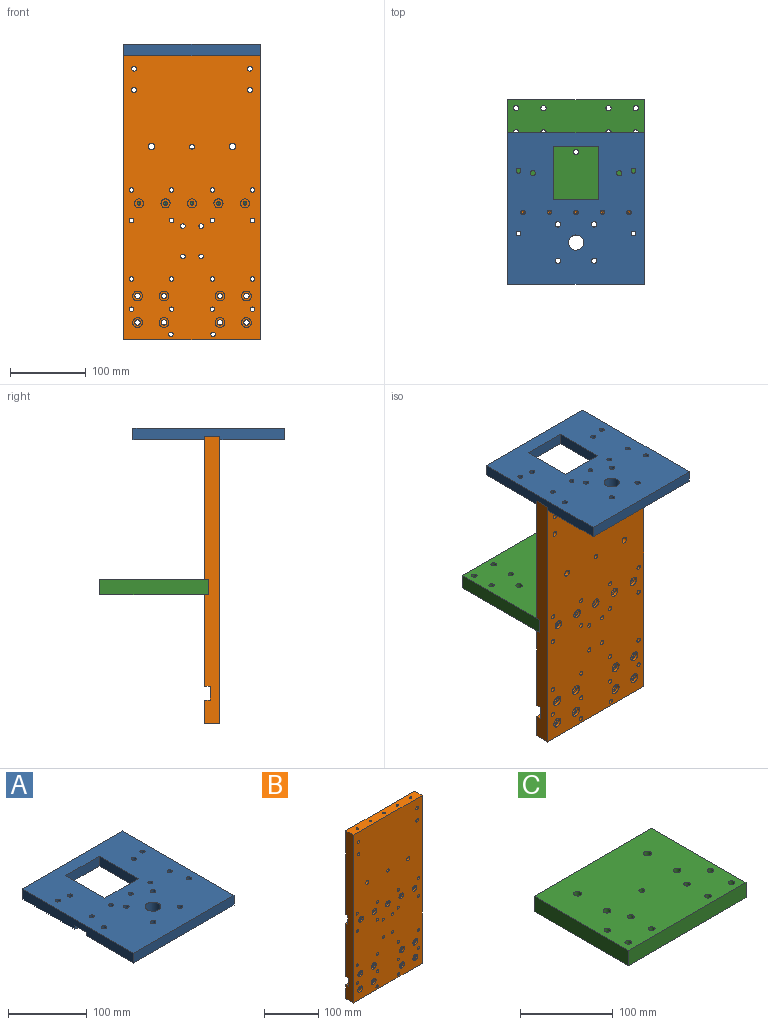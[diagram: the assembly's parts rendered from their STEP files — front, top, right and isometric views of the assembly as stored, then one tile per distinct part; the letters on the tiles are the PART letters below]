
ASSEMBLY  parts=3 mates=1
PART A: 30 faces, bbox 180x200x15 mm
  f0: plane 180x95mm, normal (0,0,-1), area 12761mm2, adj f1,f3,f4,f8,f11,f12,f13,f14
  f1: plane 200x15mm, normal (-1,0,0), area 2900mm2, adj f0,f2,f4,f5,f6,f7,f8,f9
  f2: plane 180x15mm, normal (0,-1,0), area 2700mm2, adj f1,f3,f5,f6
  f3: plane 200x15mm, normal (1,0,0), area 2900mm2, adj f0,f2,f4,f5,f6,f7,f8,f9
  f4: plane 180x15mm, normal (0,1,0), area 2700mm2, adj f0,f1,f3,f5
  f5: plane 200x180mm, normal (0,0,1), area 30985.2mm2, adj f1,f2,f3,f4,f10,f11,f12,f13
  f6: plane 180x85mm, normal (0,0,-1), area 14765.5mm2, adj f1,f2,f3,f7,f10,f22,f23,f24
  f7: plane 180x5mm, normal (0,1,0), area 900mm2, adj f1,f3,f6,f9
  f8: plane 180x5mm, normal (0,-1,0), area 900mm2, adj f0,f1,f3,f9
  f9: plane 180x20mm, normal (0,0,-1), area 3458.6mm2, adj f1,f3,f7,f8,f15,f16,f17,f18
  f10: cylinder r=10mm len=20mm, axis (0,0,1), area 942.5mm2, adj f5,f6
  f11: plane 70x15mm, normal (1,0,0), area 1050mm2, adj f0,f5,f12,f14
  f12: plane 60x15mm, normal (0,1,0), area 900mm2, adj f0,f5,f11,f13
  f13: plane 70x15mm, normal (-1,0,0), area 1050mm2, adj f0,f5,f12,f14
  f14: plane 60x15mm, normal (0,-1,0), area 900mm2, adj f0,f5,f11,f13
  f15: cylinder r=3mm len=10mm, axis (0,0,-1), area 188.5mm2, adj f5,f9
  f16: cylinder r=3mm len=10mm, axis (0,0,-1), area 188.5mm2, adj f5,f9
  f17: cylinder r=3mm len=10mm, axis (0,0,-1), area 188.5mm2, adj f5,f9
  f18: cylinder r=3mm len=10mm, axis (0,0,-1), area 188.5mm2, adj f5,f9
  f19: cylinder r=3mm len=10mm, axis (0,0,-1), area 188.5mm2, adj f5,f9
  f20: cylinder r=3.4mm len=15mm, axis (0,0,1), area 320.4mm2, adj f0,f5
  f21: cylinder r=3.4mm len=15mm, axis (0,0,1), area 320.4mm2, adj f0,f5
  f22: cylinder r=3.5mm len=15mm, axis (0,0,1), area 329.9mm2, adj f5,f6
  f23: cylinder r=3.5mm len=15mm, axis (0,0,1), area 329.9mm2, adj f5,f6
  f24: cylinder r=3.5mm len=15mm, axis (0,0,1), area 329.9mm2, adj f5,f6
  f25: cylinder r=3.5mm len=15mm, axis (0,0,1), area 329.9mm2, adj f5,f6
  f26: cylinder r=3.25mm len=15mm, axis (0,0,-1), area 306.3mm2, adj f0,f5
  f27: cylinder r=3.25mm len=15mm, axis (0,0,-1), area 306.3mm2, adj f0,f5
  f28: cylinder r=3.25mm len=15mm, axis (0,0,-1), area 306.3mm2, adj f5,f6
  f29: cylinder r=3.25mm len=15mm, axis (0,0,-1), area 306.3mm2, adj f5,f6
PART B: 92 faces, bbox 180x20x380 mm
  f0: plane 180x31mm, normal (0,1,0), area 5369.5mm2, adj f3,f5,f9,f15,f24,f27,f33,f36
  f1: plane 180x121mm, normal (0,1,0), area 21286.8mm2, adj f3,f5,f6,f7,f8,f10,f12,f16
  f2: plane 190x180mm, normal (0,1,0), area 33807.5mm2, adj f3,f4,f5,f13,f57,f58,f61,f63
  f3: plane 380x20mm, normal (1,0,0), area 7374mm2, adj f0,f1,f2,f4,f9,f11,f12,f13
  f4: plane 180x20mm, normal (0,0,1), area 3520.5mm2, adj f2,f3,f5,f11,f81,f83,f85,f87
  f5: plane 380x20mm, normal (-1,0,0), area 7374mm2, adj f0,f1,f2,f4,f9,f11,f12,f13
  f6: cylinder r=3mm len=20mm, axis (0,1,0), area 377mm2, adj f1,f11
  f7: cylinder r=3mm len=20mm, axis (0,1,0), area 377mm2, adj f1,f11
  f8: cylinder r=3mm len=20mm, axis (0,1,0), area 377mm2, adj f1,f11
  f9: plane 180x20mm, normal (0,0,-1), area 3600mm2, adj f0,f3,f5,f11
  f10: cylinder r=3mm len=20mm, axis (0,1,0), area 377mm2, adj f1,f11
  f11: plane 380x180mm, normal (0,-1,0), area 65871.2mm2, adj f3,f4,f5,f6,f7,f8,f9,f10
  f12: plane 180x5mm, normal (0,0,1), area 900mm2, adj f1,f3,f5,f14
  f13: plane 180x5mm, normal (0,0,-1), area 900mm2, adj f2,f3,f5,f14
  f14: plane 180x20mm, normal (0,1,0), area 3501.8mm2, adj f3,f5,f12,f13,f42,f45,f48,f51
  f15: plane 180x7mm, normal (0,0,1), area 1260mm2, adj f0,f3,f5,f17
  f16: plane 180x7mm, normal (0,0,-1), area 1260mm2, adj f1,f3,f5,f17
  f17: plane 180x18mm, normal (0,1,0), area 3126.9mm2, adj f3,f5,f15,f16,f66,f67,f70,f72
  f18: cylinder r=3.5mm len=16mm, axis (0,-1,0), area 351.9mm2, adj f1,f19
  f19: plane 13x13mm, normal (0,-1,0), area 94.2mm2, adj f18,f20
  f20: cylinder r=6.5mm len=13mm, axis (0,-1,0), area 163.4mm2, adj f11,f19
  f21: cylinder r=3.5mm len=16mm, axis (0,-1,0), area 351.9mm2, adj f1,f22
  f22: plane 13x13mm, normal (0,-1,0), area 94.2mm2, adj f21,f23
  f23: cylinder r=6.5mm len=13mm, axis (0,-1,0), area 163.4mm2, adj f11,f22
  f24: cylinder r=3.5mm len=16mm, axis (0,-1,0), area 351.9mm2, adj f0,f25
  f25: plane 13x13mm, normal (0,-1,0), area 94.2mm2, adj f24,f26
  f26: cylinder r=6.5mm len=13mm, axis (0,-1,0), area 163.4mm2, adj f11,f25
  f27: cylinder r=3.5mm len=16mm, axis (0,-1,0), area 351.9mm2, adj f0,f28
  f28: plane 13x13mm, normal (0,-1,0), area 94.2mm2, adj f27,f29
  f29: cylinder r=6.5mm len=13mm, axis (0,-1,0), area 163.4mm2, adj f11,f28
  f30: cylinder r=3.5mm len=16mm, axis (0,-1,0), area 351.9mm2, adj f1,f31
  f31: plane 13x13mm, normal (0,-1,0), area 94.2mm2, adj f30,f32
  f32: cylinder r=6.5mm len=13mm, axis (0,-1,0), area 163.4mm2, adj f11,f31
  f33: cylinder r=3.5mm len=16mm, axis (0,-1,0), area 351.9mm2, adj f0,f34
  f34: plane 13x13mm, normal (0,-1,0), area 94.2mm2, adj f33,f35
  f35: cylinder r=6.5mm len=13mm, axis (0,-1,0), area 163.4mm2, adj f11,f34
  f36: cylinder r=3.5mm len=16mm, axis (0,-1,0), area 351.9mm2, adj f0,f37
  f37: plane 13x13mm, normal (0,-1,0), area 94.2mm2, adj f36,f38
  f38: cylinder r=6.5mm len=13mm, axis (0,-1,0), area 163.4mm2, adj f11,f37
  f39: cylinder r=3.5mm len=16mm, axis (0,-1,0), area 351.9mm2, adj f1,f40
  f40: plane 13x13mm, normal (0,-1,0), area 94.2mm2, adj f39,f41
  f41: cylinder r=6.5mm len=13mm, axis (0,-1,0), area 163.4mm2, adj f11,f40
  f42: cylinder r=2.5mm len=11mm, axis (0,-1,0), area 172.8mm2, adj f14,f43
  f43: plane 12x12mm, normal (0,-1,0), area 93.5mm2, adj f42,f44
  f44: cylinder r=6mm len=12mm, axis (0,-1,0), area 150.8mm2, adj f11,f43
  f45: cylinder r=2.5mm len=11mm, axis (0,-1,0), area 172.8mm2, adj f14,f46
  f46: plane 12x12mm, normal (0,-1,0), area 93.5mm2, adj f45,f47
  f47: cylinder r=6mm len=12mm, axis (0,-1,0), area 150.8mm2, adj f11,f46
  f48: cylinder r=2.5mm len=11mm, axis (0,-1,0), area 172.8mm2, adj f14,f49
  f49: plane 12x12mm, normal (0,-1,0), area 93.5mm2, adj f48,f50
  f50: cylinder r=6mm len=12mm, axis (0,-1,0), area 150.8mm2, adj f11,f49
  f51: cylinder r=2.5mm len=11mm, axis (0,-1,0), area 172.8mm2, adj f14,f52
  f52: plane 12x12mm, normal (0,-1,0), area 93.5mm2, adj f51,f53
  f53: cylinder r=6mm len=12mm, axis (0,-1,0), area 150.8mm2, adj f11,f52
  f54: cylinder r=2.5mm len=11mm, axis (0,-1,0), area 172.8mm2, adj f14,f55
  f55: plane 12x12mm, normal (0,-1,0), area 93.5mm2, adj f54,f56
  f56: cylinder r=6mm len=12mm, axis (0,-1,0), area 150.8mm2, adj f11,f55
  f57: cylinder r=3mm len=20mm, axis (0,-1,0), area 377mm2, adj f2,f11
  f58: cylinder r=3mm len=20mm, axis (0,-1,0), area 377mm2, adj f2,f11
  f59: cylinder r=3mm len=20mm, axis (0,-1,0), area 377mm2, adj f1,f11
  f60: cylinder r=3mm len=20mm, axis (0,-1,0), area 377mm2, adj f1,f11
  f61: cylinder r=3mm len=20mm, axis (0,-1,0), area 377mm2, adj f2,f11
  f62: cylinder r=3mm len=20mm, axis (0,-1,0), area 377mm2, adj f1,f11
  f63: cylinder r=3mm len=20mm, axis (0,-1,0), area 377mm2, adj f2,f11
  f64: cylinder r=3mm len=20mm, axis (0,-1,0), area 377mm2, adj f1,f11
  f65: cylinder r=3mm len=20mm, axis (0,-1,0), area 377mm2, adj f1,f11
  f66: cylinder r=3mm len=13mm, axis (0,-1,0), area 245mm2, adj f11,f17
  f67: cylinder r=3mm len=13mm, axis (0,-1,0), area 245mm2, adj f11,f17
  f68: cylinder r=3mm len=20mm, axis (0,-1,0), area 377mm2, adj f1,f11
  f69: cylinder r=3mm len=20mm, axis (0,-1,0), area 377mm2, adj f1,f11
  f70: cylinder r=3mm len=13mm, axis (0,-1,0), area 245mm2, adj f11,f17
  f71: cylinder r=3mm len=20mm, axis (0,-1,0), area 377mm2, adj f1,f11
  f72: cylinder r=3mm len=13mm, axis (0,-1,0), area 245mm2, adj f11,f17
  f73: cylinder r=3mm len=20mm, axis (0,1,0), area 377mm2, adj f0,f11
  f74: cylinder r=3mm len=20mm, axis (0,1,0), area 377mm2, adj f0,f11
  f75: cylinder r=3.25mm len=20mm, axis (0,1,0), area 408.4mm2, adj f2,f11
  f76: cylinder r=3.25mm len=20mm, axis (0,1,0), area 408.4mm2, adj f2,f11
  f77: cylinder r=3.25mm len=20mm, axis (0,1,0), area 408.4mm2, adj f2,f11
  f78: cylinder r=3.25mm len=20mm, axis (0,1,0), area 408.4mm2, adj f2,f11
  f79: cylinder r=3.25mm len=20mm, axis (0,1,0), area 408.4mm2, adj f2,f11
  f80: cone r=0mm half-angle=59deg, axis (0,0,1), area 18.6mm2, adj f81
  f81: cylinder r=2.25mm len=20mm, axis (0,0,1), area 282.7mm2, adj f4,f80
  f82: cone r=0mm half-angle=59deg, axis (0,0,1), area 18.6mm2, adj f83
  f83: cylinder r=2.25mm len=20mm, axis (0,0,1), area 282.7mm2, adj f4,f82
  f84: cone r=0mm half-angle=59deg, axis (0,0,1), area 18.6mm2, adj f85
  f85: cylinder r=2.25mm len=20mm, axis (0,0,1), area 282.7mm2, adj f4,f84
  f86: cone r=0mm half-angle=59deg, axis (0,0,1), area 18.6mm2, adj f87
  f87: cylinder r=2.25mm len=20mm, axis (0,0,1), area 282.7mm2, adj f4,f86
  f88: cone r=0mm half-angle=59deg, axis (0,0,1), area 18.6mm2, adj f89
  f89: cylinder r=2.25mm len=20mm, axis (0,0,1), area 282.7mm2, adj f4,f88
  f90: cylinder r=4.25mm len=20mm, axis (0,-1,0), area 534.1mm2, adj f2,f11
  f91: cylinder r=4.25mm len=20mm, axis (0,-1,0), area 534.1mm2, adj f2,f11
PART C: 29 faces, bbox 180x144x20 mm
  f0: plane 144x20mm, normal (1,0,0), area 2880mm2, adj f1,f3,f4,f5
  f1: plane 180x20mm, normal (0,1,0), area 3520.5mm2, adj f0,f2,f4,f5,f16,f18,f20,f22
  f2: plane 144x20mm, normal (-1,0,0), area 2880mm2, adj f1,f3,f4,f5
  f3: plane 180x20mm, normal (0,-1,0), area 3600mm2, adj f0,f2,f4,f5
  f4: plane 180x144mm, normal (0,0,1), area 25352mm2, adj f0,f1,f2,f3,f6,f7,f8,f9
  f5: plane 180x144mm, normal (0,0,-1), area 25352mm2, adj f0,f1,f2,f3,f6,f7,f8,f9
  f6: cylinder r=3.5mm len=20mm, axis (0,0,1), area 439.8mm2, adj f4,f5
  f7: cylinder r=3.5mm len=20mm, axis (0,0,1), area 439.8mm2, adj f4,f5
  f8: cylinder r=3.5mm len=20mm, axis (0,0,1), area 439.8mm2, adj f4,f5
  f9: cylinder r=3.5mm len=20mm, axis (0,0,1), area 439.8mm2, adj f4,f5
  f10: cylinder r=3.5mm len=20mm, axis (0,0,1), area 439.8mm2, adj f4,f5
  f11: cylinder r=3.5mm len=20mm, axis (0,0,1), area 439.8mm2, adj f4,f5
  f12: cylinder r=3.5mm len=20mm, axis (0,0,1), area 439.8mm2, adj f4,f5
  f13: cylinder r=3.5mm len=20mm, axis (0,0,1), area 439.8mm2, adj f4,f5
  f14: cylinder r=3.25mm len=20mm, axis (0,0,1), area 408.4mm2, adj f4,f5
  f15: cone r=0mm half-angle=59deg, axis (0,1,0), area 18.6mm2, adj f16
  f16: cylinder r=2.25mm len=15mm, axis (0,1,0), area 212.1mm2, adj f1,f15
  f17: cone r=0mm half-angle=59deg, axis (0,1,0), area 18.6mm2, adj f18
  f18: cylinder r=2.25mm len=15mm, axis (0,1,0), area 212.1mm2, adj f1,f17
  f19: cone r=0mm half-angle=59deg, axis (0,1,0), area 18.6mm2, adj f20
  f20: cylinder r=2.25mm len=15mm, axis (0,1,0), area 212.1mm2, adj f1,f19
  f21: cone r=0mm half-angle=59deg, axis (0,1,0), area 18.6mm2, adj f22
  f22: cylinder r=2.25mm len=15mm, axis (0,1,0), area 212.1mm2, adj f1,f21
  f23: cone r=0mm half-angle=59deg, axis (0,1,0), area 18.6mm2, adj f24
  f24: cylinder r=2.25mm len=15mm, axis (0,1,0), area 212.1mm2, adj f1,f23
  f25: cylinder r=4.25mm len=20mm, axis (0,0,1), area 534.1mm2, adj f4,f5
  f26: cylinder r=4.25mm len=20mm, axis (0,0,1), area 534.1mm2, adj f4,f5
  f27: cylinder r=4.25mm len=20mm, axis (0,0,1), area 534.1mm2, adj f4,f5
  f28: cylinder r=4.25mm len=20mm, axis (0,0,1), area 534.1mm2, adj f4,f5
PLACE A t=(-134.98,-25.97,268.81)mm
PLACE B t=(-134.98,-12.05,14.61)mm
PLACE C rot(axis=(1,0,0),180deg) t=(-134.98,86.61,83.81)mm
MATE fastened C.f19 <-> B.f48  axis (0,-1,0) through (-134.98,-17.05,73.81)mm
